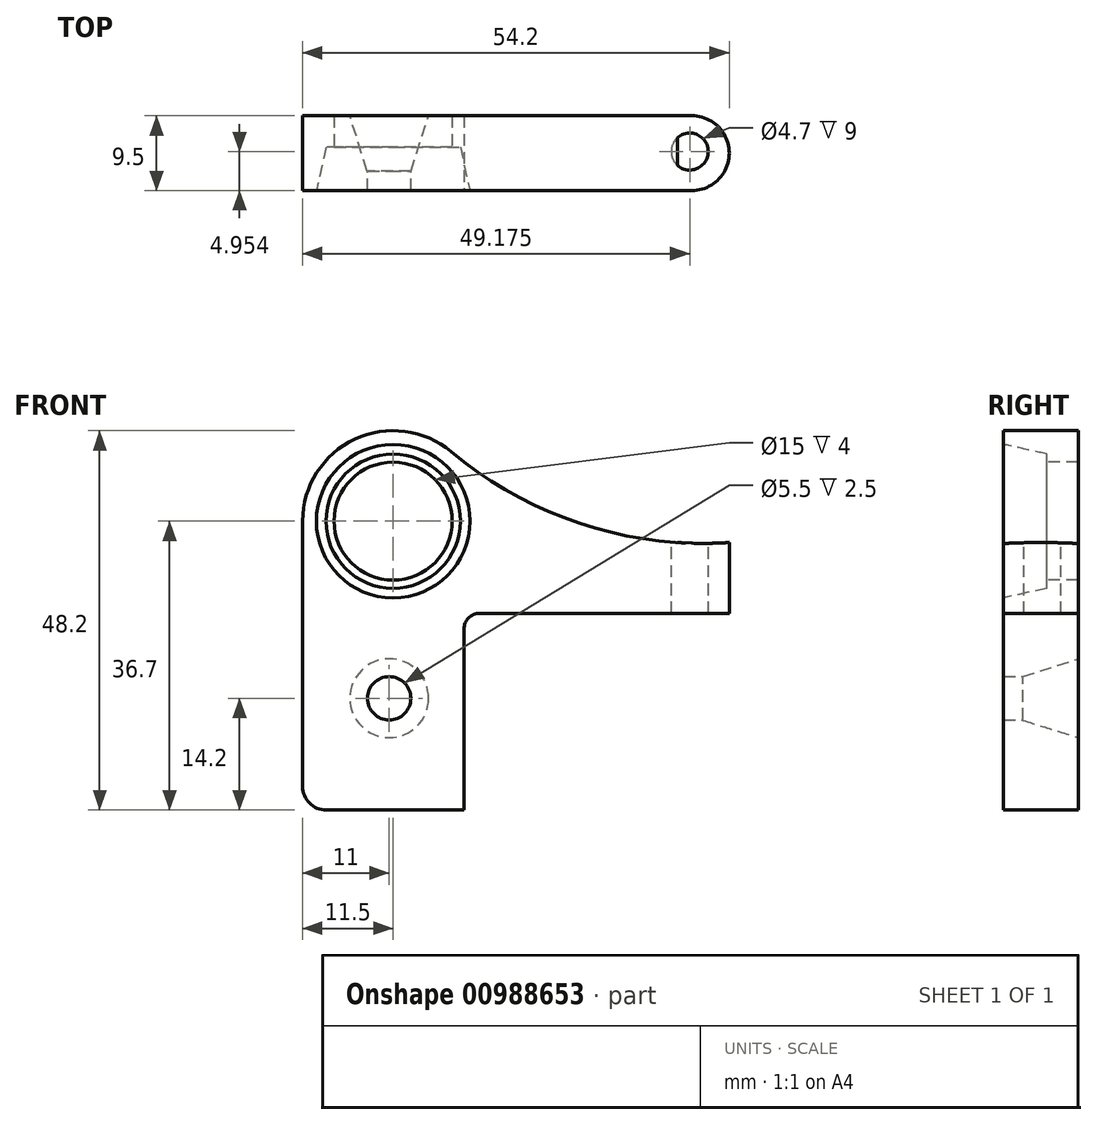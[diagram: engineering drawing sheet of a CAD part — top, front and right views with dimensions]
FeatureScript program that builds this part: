
annotation { "Feature Type Name" : "Feature", "Feature Type Description" : "" }
export const myFeature = defineFeature(function(context is Context, id is Id, definition is map)
    precondition{}
    {
        {
            var Q0;
            Q0=qCreatedBy(makeId("Front.planeOp"),FACE);
            var sketch = newSketch(context, id + "F0", { "sketchPlane" : qUnion([Q0])});
            skLineSegment(sketch, "E0", {"start": v(0, 0) * mm, "end": v(0, 36.7) * mm});
            skLineSegment(sketch, "E1", {"start": v(54.2, 36.7) * mm, "end": v(54.2, 36.6) * mm});
            skLineSegment(sketch, "E2", {"start": v(54.2, 24.99) * mm, "end": v(20.5, 24.99) * mm});
            skLineSegment(sketch, "E3", {"start": v(20.5, 24.99) * mm, "end": v(20.5, 0) * mm});
            skLineSegment(sketch, "E4", {"start": v(20.5, 0) * mm, "end": v(0, 0) * mm});
            skPoint(sketch, "E5.orphan", {"position": v(54.2, 48.2) * mm});
            skLineSegment(sketch, "E6.trimOffspring", {"start": v(54.2, 33.99) * mm, "end": v(54.2, 24.99) * mm});
            skArc(sketch, "E7", {"start": v(18.88, 45.52) * mm, "mid": v(6.63, 47.12) * mm, "end": v(0, 36.7) * mm});
            skArc(sketch, "E8", {"start": v(18.88, 45.52) * mm, "mid": v(35.43, 36.34) * mm, "end": v(54.2, 33.99) * mm});
            skPoint(sketch, "E8.first.point", {"position": v(18.88, 45.52) * mm});
            skPoint(sketch, "E8.third.point", {"position": v(35.73, 131.25) * mm});
            skPoint(sketch, "E9.orphan", {"position": v(23, 48.2) * mm});
            skPoint(sketch, "E10.orphan", {"position": v(0, 48.2) * mm});
            skSolve(sketch);
        }
        {
            var Q0;
            Q0=makeQuery(id+"F0.imprint","IMPRINT",FACE,{"disambiguationData":[TD([[makeQuery(id+"F0.imprint","IMPRINT",EDGE,{"derivedFrom":sQuery(id+"F0.wireOp",EDGE,"E0")}),-1.0]])]});
            extrude(context, id + "F1", {"entities" : qUnion([Q0]), "oppositeDirection" : true, "depth" : 9.5 * mm, "offsetDistance" : 25 * mm});
        }
        {
            var Q0;
            Q0=qCreatedBy(makeId("Front.planeOp"),FACE);
            var sketch = newSketch(context, id + "F2", { "sketchPlane" : qUnion([Q0])});
            skCircle(sketch, "E11", {"center": v(11.5, 36.7) * mm, "radius": 7.5 * mm});
            skSolve(sketch);
        }
        {
            var Q0;
            Q0=makeQuery(id+"F2.imprint","IMPRINT",FACE,{"disambiguationData":[TD([[makeQuery(id+"F2.imprint","IMPRINT",EDGE,{"derivedFrom":sQuery(id+"F2.wireOp",EDGE,"E11")}),1.0]])]});
            extrude(context, id + "F3", {"entities" : qUnion([Q0]), "operationType" : NewBodyOperationType.REMOVE, "oppositeDirection" : true, "depth" : 9.5 * mm, "offsetDistance" : 25 * mm});
        }
        {
            var Q0;
            Q0=qCreatedBy(makeId("Front.planeOp"),FACE);
            var sketch = newSketch(context, id + "F4", { "sketchPlane" : qUnion([Q0])});
            skCircle(sketch, "E12", {"center": v(11.5, 36.7) * mm, "radius": 8.5 * mm});
            skSolve(sketch);
        }
        {
            var Q0;
            Q0=makeQuery(id+"F4.imprint","IMPRINT",FACE,{"disambiguationData":[TD([[makeQuery(id+"F4.imprint","IMPRINT",EDGE,{"derivedFrom":sQuery(id+"F4.wireOp",EDGE,"E12")}),1.0]])]});
            extrude(context, id + "F5", {"entities" : qUnion([Q0]), "operationType" : NewBodyOperationType.REMOVE, "oppositeDirection" : true, "depth" : 5.5 * mm, "offsetDistance" : 25 * mm});
        }
        {
            var Q0;
            Q0=qCreatedBy(makeId("Front.planeOp"),FACE);
            var sketch = newSketch(context, id + "F6", { "sketchPlane" : qUnion([Q0])});
            skCircle(sketch, "E13", {"center": v(11.5, 36.7) * mm, "radius": 9.75 * mm});
            skSolve(sketch);
        }
        {
            var Q0;
            Q0=makeQuery(id+"F6.imprint","IMPRINT",FACE,{"disambiguationData":[TD([[makeQuery(id+"F6.imprint","IMPRINT",EDGE,{"derivedFrom":sQuery(id+"F6.wireOp",EDGE,"E13")}),1.0]])]});
            extrude(context, id + "F7", {"entities" : qUnion([Q0]), "operationType" : NewBodyOperationType.REMOVE, "oppositeDirection" : true, "depth" : 5.5 * mm, "offsetDistance" : 25 * mm, "hasDraft" : true, "draftAngle" : 12.5 * degree, "draftPullDirection" : true, "hasSecondDirection" : true, "secondDirectionOppositeDirection" : false, "secondDirectionDepth" : 25 * mm});
        }
        {
            var Q0;
            Q0=makeQuery(id+"F1.opExtrude","CAP_EDGE",EDGE,{"disambiguationData":[OSD([sQuery(id+"F0.wireOp",EDGE,"E6.trimOffspring")])],"isStart":true});
            fillet(context, id + "F8", {"entities" : qUnion([Q0]), "radius" : 4.75 * mm, "tangentPropagation" : true, "allowEdgeOverflow" : false});
        }
        {
            var Q0;
            Q0=makeQuery(id+"F1.opExtrude","CAP_EDGE",EDGE,{"disambiguationData":[OSD([sQuery(id+"F0.wireOp",EDGE,"E6.trimOffspring")])],"isStart":false});
            fillet(context, id + "F9", {"entities" : qUnion([Q0]), "radius" : 4.75 * mm, "tangentPropagation" : true, "allowEdgeOverflow" : false});
        }
        {
            var Q0;
            Q0=makeQuery(id+"F1.opExtrude","SWEPT_EDGE",EDGE,{"disambiguationData":[OSD([sQuery(id+"F0.wireOp",EDGE,"E0"),sQuery(id+"F0.wireOp",EDGE,"E4")])]});
            fillet(context, id + "F10", {"entities" : qUnion([Q0]), "radius" : 3 * mm, "tangentPropagation" : true, "allowEdgeOverflow" : false});
        }
        {
            var Q0;
            Q0=makeQuery(id+"F1.opExtrude","SWEPT_EDGE",EDGE,{"disambiguationData":[OSD([sQuery(id+"F0.wireOp",EDGE,"E2"),sQuery(id+"F0.wireOp",EDGE,"E3")])]});
            fillet(context, id + "F11", {"entities" : qUnion([Q0]), "radius" : 2 * mm, "tangentPropagation" : true, "allowEdgeOverflow" : false});
        }
        {
            var Q0;
            Q0=qCreatedBy(makeId("Top.planeOp"),FACE);
            var Q1;
            {var subQ0=sQuery(id+"F0.wireOp",EDGE,"E6.trimOffspring");Q1=makeQuery(id+"F9.opFillet","BLEND_VERTEX",VERTEX,{"blendedFrom":[makeQuery(id+"F1.opExtrude","CAP_EDGE",EDGE,{"disambiguationData":[OSD([subQ0])],"isStart":false}),makeQuery(id+"F8.opFillet","BLEND_FACE",FACE,{"disambiguationData":[OSD([subQ0])]}),makeQuery(id+"F1.opExtrude","SWEPT_FACE",FACE,{"disambiguationData":[OSD([sQuery(id+"F0.wireOp",EDGE,"E8")])]})],"blendedInto":[makeQuery(id+"F8.opFillet","BLEND_FACE",FACE,{"disambiguationData":[OSD([subQ0])]}),makeQuery(id+"F1.opExtrude","SWEPT_FACE",FACE,{"disambiguationData":[OSD([sQuery(id+"F0.wireOp",EDGE,"E8")])]})]});}
            cPlane(context, id + "F12", {"entities" : qUnion([Q0, Q1]), "cplaneType" : CPlaneType.PLANE_POINT, "offset" : 40.5 * mm, "width" : 150 * mm, "height" : 150 * mm});
        }
        {
            var Q0;
            Q0=qCreatedBy(id+"F12.planeOp",FACE);
            var sketch = newSketch(context, id + "F13", { "sketchPlane" : qUnion([Q0])});
            skCircle(sketch, "E14", {"center": v(49.18, 4.95) * mm, "radius": 2.35 * mm});
            skSolve(sketch);
        }
        {
            var Q0;
            Q0=makeQuery(id+"F13.imprint","IMPRINT",FACE,{"disambiguationData":[TD([[makeQuery(id+"F13.imprint","IMPRINT",EDGE,{"derivedFrom":sQuery(id+"F13.wireOp",EDGE,"E14")}),1.0]])]});
            extrude(context, id + "F14", {"entities" : qUnion([Q0]), "operationType" : NewBodyOperationType.REMOVE, "oppositeDirection" : true, "depth" : 10 * mm, "offsetDistance" : 25 * mm});
        }
        {
            var Q0;
            Q0=qCreatedBy(makeId("Front.planeOp"),FACE);
            cPlane(context, id + "F15", {"entities" : qUnion([Q0]), "cplaneType" : CPlaneType.OFFSET, "offset" : 9.5 * mm, "oppositeDirection" : true, "width" : 150 * mm, "height" : 150 * mm});
        }
        {
            var Q0;
            Q0=qCreatedBy(id+"F15.planeOp",FACE);
            var sketch = newSketch(context, id + "F16", { "sketchPlane" : qUnion([Q0])});
            skCircle(sketch, "E15", {"center": v(11, 14.2) * mm, "radius": 2.75 * mm});
            skSolve(sketch);
        }
        {
            var Q0;
            Q0=makeQuery(id+"F16.imprint","IMPRINT",FACE,{"disambiguationData":[TD([[makeQuery(id+"F16.imprint","IMPRINT",EDGE,{"derivedFrom":sQuery(id+"F16.wireOp",EDGE,"E15")}),1.0]])]});
            extrude(context, id + "F17", {"entities" : qUnion([Q0]), "operationType" : NewBodyOperationType.REMOVE, "depth" : 9.5 * mm, "offsetDistance" : 25 * mm});
        }
        {
            var Q0;
            Q0=qCreatedBy(id+"F15.planeOp",FACE);
            var sketch = newSketch(context, id + "F18", { "sketchPlane" : qUnion([Q0])});
            skCircle(sketch, "E16", {"center": v(11, 14.2) * mm, "radius": 5 * mm});
            skSolve(sketch);
        }
        {
            var Q0;
            Q0=makeQuery(id+"F18.imprint","IMPRINT",FACE,{"disambiguationData":[TD([[makeQuery(id+"F18.imprint","IMPRINT",EDGE,{"derivedFrom":sQuery(id+"F18.wireOp",EDGE,"E16")}),1.0]])]});
            extrude(context, id + "F19", {"entities" : qUnion([Q0]), "operationType" : NewBodyOperationType.REMOVE, "depth" : 7 * mm, "offsetDistance" : 25 * mm, "hasDraft" : true, "draftAngle" : 17.5 * degree, "draftPullDirection" : true, "hasSecondDirection" : true, "secondDirectionOppositeDirection" : true, "secondDirectionDepth" : 7 * mm});
        }
    });
